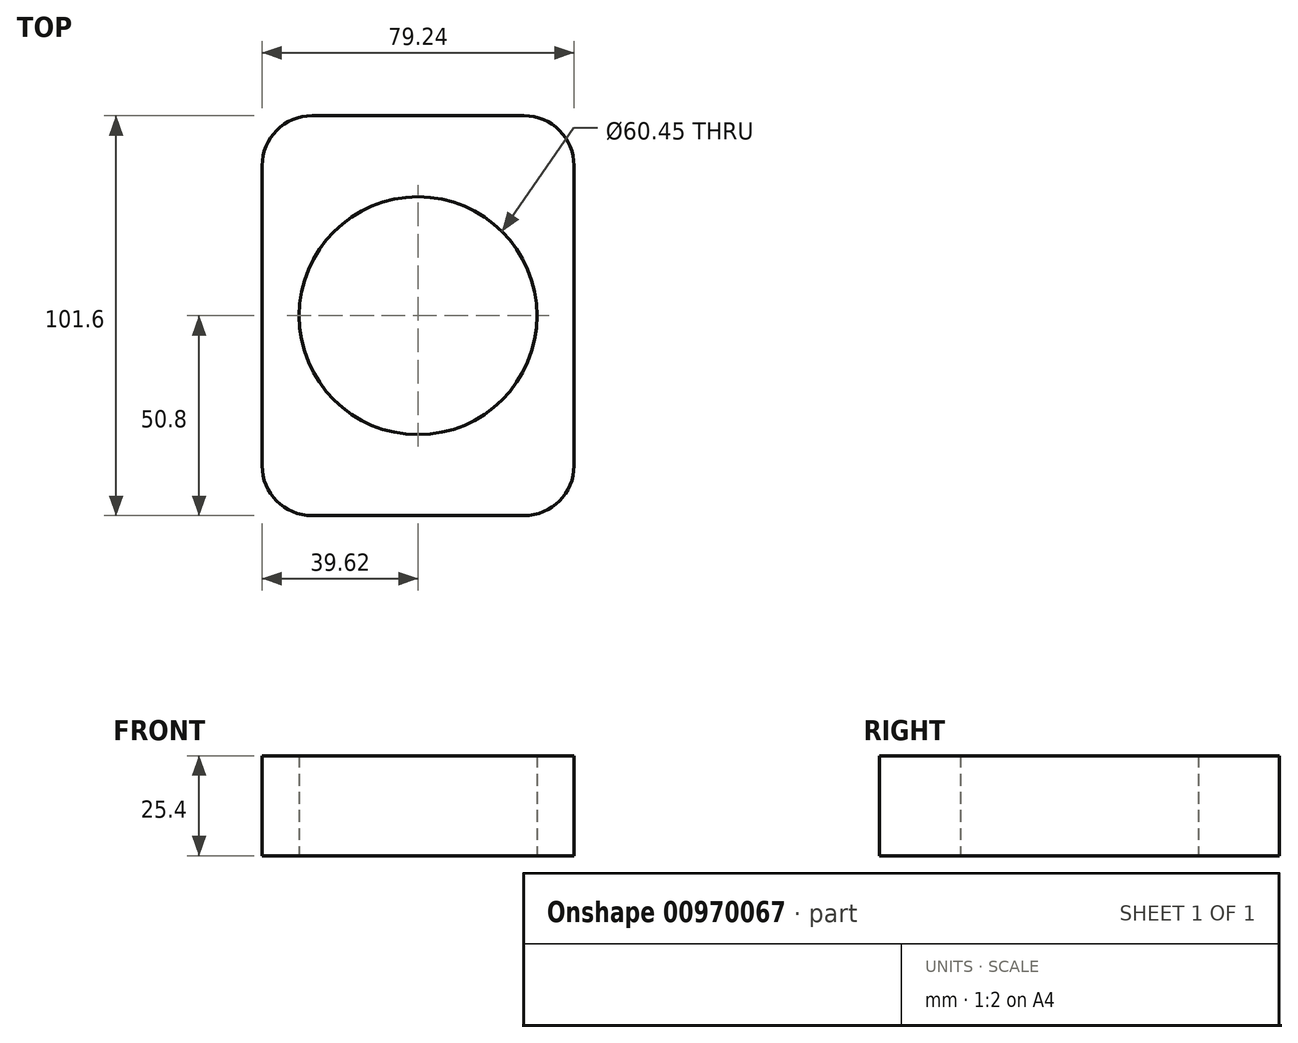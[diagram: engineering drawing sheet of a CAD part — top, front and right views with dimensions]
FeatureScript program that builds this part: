
annotation { "Feature Type Name" : "Feature", "Feature Type Description" : "" }
export const myFeature = defineFeature(function(context is Context, id is Id, definition is map)
    precondition{}
    {
        {
            var Q0;
            Q0=qCreatedBy(makeId("Top.planeOp"),FACE);
            var sketch = newSketch(context, id + "F0", { "sketchPlane" : qUnion([Q0])});
            skCircle(sketch, "E0", {"center": v(0, 0) * mm, "radius": 30.23 * mm});
            skLineSegment(sketch, "E1.bottom", {"start": v(-26.92, -50.8) * mm, "end": v(26.92, -50.8) * mm});
            skLineSegment(sketch, "E1.top", {"start": v(-26.92, 50.8) * mm, "end": v(26.92, 50.8) * mm});
            skLineSegment(sketch, "E1.left", {"start": v(-39.62, -38.1) * mm, "end": v(-39.62, 38.1) * mm});
            skLineSegment(sketch, "E1.right", {"start": v(39.62, -38.1) * mm, "end": v(39.62, 38.1) * mm});
            skPoint(sketch, "E2.visualSharp", {"position": v(-39.62, 50.8) * mm});
            skArc(sketch, "E2.filletArc", {"start": v(-26.92, 50.8) * mm, "mid": v(-35.9, 47.08) * mm, "end": v(-39.62, 38.1) * mm});
            skPoint(sketch, "E3.visualSharp", {"position": v(39.62, 50.8) * mm});
            skArc(sketch, "E3.filletArc", {"start": v(39.62, 38.1) * mm, "mid": v(35.9, 47.08) * mm, "end": v(26.92, 50.8) * mm});
            skPoint(sketch, "E4.visualSharp", {"position": v(39.62, -50.8) * mm});
            skArc(sketch, "E4.filletArc", {"start": v(26.92, -50.8) * mm, "mid": v(35.9, -47.08) * mm, "end": v(39.62, -38.1) * mm});
            skPoint(sketch, "E5.visualSharp", {"position": v(-39.62, -50.8) * mm});
            skArc(sketch, "E5.filletArc", {"start": v(-39.62, -38.1) * mm, "mid": v(-35.9, -47.08) * mm, "end": v(-26.92, -50.8) * mm});
            skSolve(sketch);
        }
        {
            var Q0;
            Q0 = qSketchRegion(id + "F0", true);
            extrude(context, id + "F1", {"entities" : qUnion([Q0]), "depth" : 25.4 * mm, "offsetDistance" : 25.4 * mm});
        }
    });
